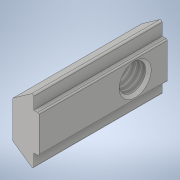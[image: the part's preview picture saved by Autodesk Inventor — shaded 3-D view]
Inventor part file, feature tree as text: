
AUTODESK INVENTOR PART (.ipt)
format: ipt  version: 2021.4 (Build 254397000, 397)  size: 149,504 bytes
history: native  units: mm
features: other x28, sketch x2, extrude x1, revolve x1, thread x1
ambient origin geometry x8: Origin, YZ Plane, XZ Plane, XY Plane, X Axis, Y Axis, Z Axis, Center Point
bodies: Solid1 (feature_tree)
feature tree (33):
  extrude  "Extrusion1"  TaperAngle=360.0deg  [1 undecoded]
  revolve  "Revolution1"  [1 undecoded]
  thread  "Thread1"  [1 undecoded]
  other  "nut_XY"
  other  "nut_YZ"
  other  "nut_ZX"
  other  "nut_X"
  other  "nut_Y"
  other  "nut_Z"
  other  "nut_Center"
  other  "to_bolt_XY"
  other  "to_bolt_YZ"
  other  "to_bolt_ZX"
  other  "to_bolt_X"
  other  "to_bolt_Y"
  other  "to_bolt_Z"
  other  "to_bolt_Center"
  other  "to_frames_XY"
  other  "to_frames_YZ"
  other  "to_frames_ZX"
  other  "to_frames_X"
  other  "to_frames_Y"
  other  "to_frames_Z"
  other  "to_frames_Center"
  other  "to_lane_XY"
  other  "to_lane_YZ"
  other  "to_lane_ZX"
  other  "to_lane_X"
  other  "to_lane_Y"
  other  "to_lane_Z"
  other  "to_lane_Center"
  sketch  "Sketch_2"  dims[d0=15.0mm d1=0.0mm d2=360.0deg]
  sketch  "Sketch_5"  dims[d3=3.234mm d4=0.0mm d5=0.0mm d6=0.0mm d7=5.0mm d8=0.0mm]
note: 3 required parameter values undecoded (feature->parameter linkage not recoverable at this tier; creation-order binding heuristic only, values carry confidence <= 0.55)